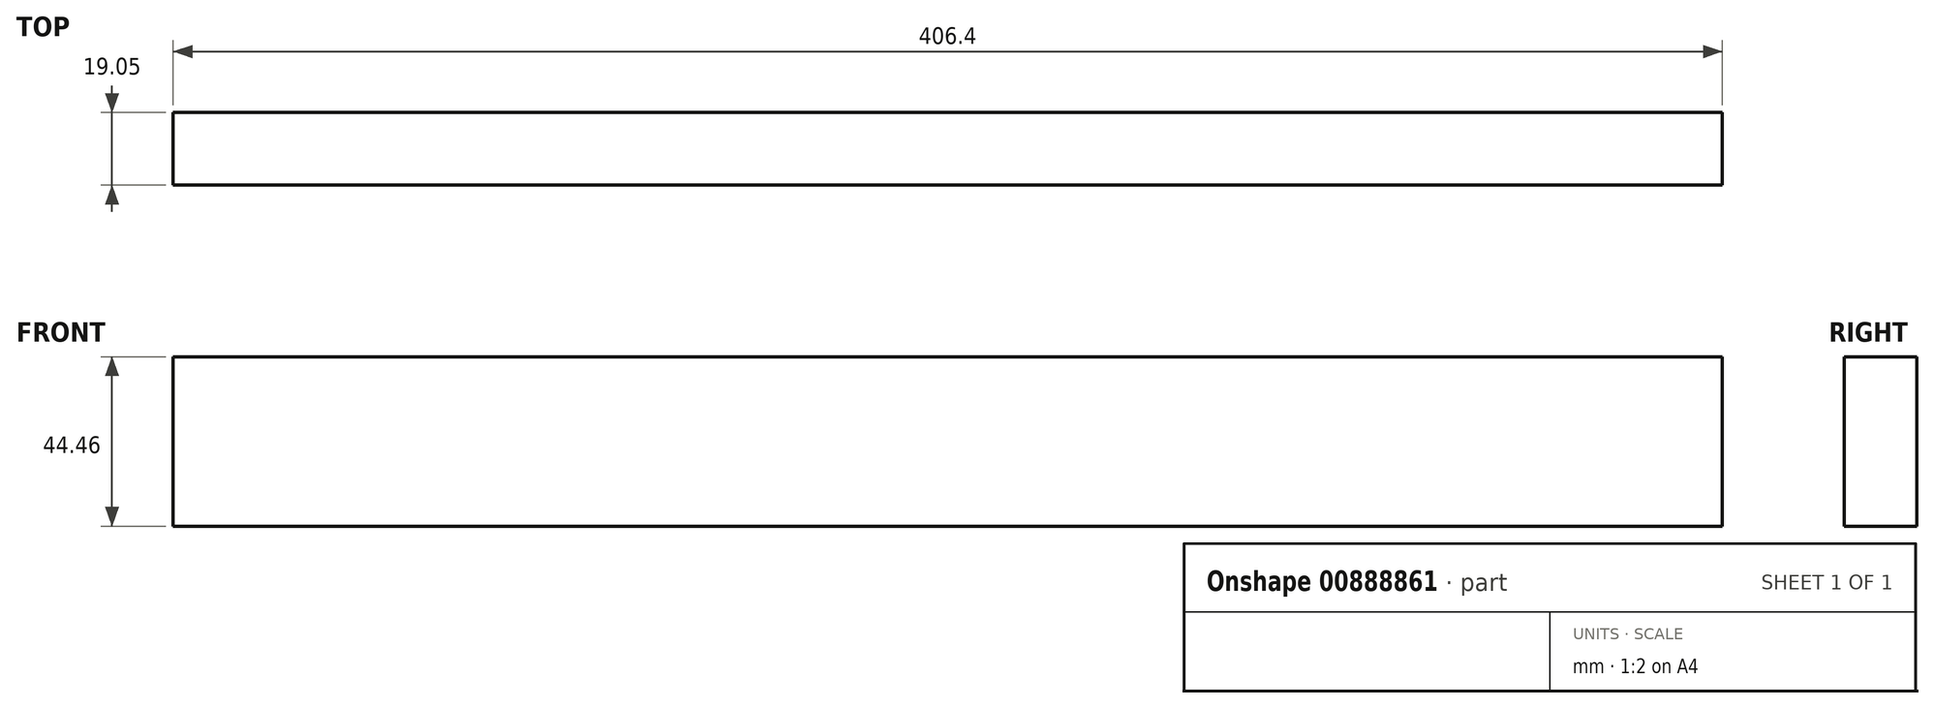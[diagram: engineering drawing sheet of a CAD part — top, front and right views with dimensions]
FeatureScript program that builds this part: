
annotation { "Feature Type Name" : "Feature", "Feature Type Description" : "" }
export const myFeature = defineFeature(function(context is Context, id is Id, definition is map)
    precondition{}
    {
        {
            var Q0;
            Q0=qCreatedBy(makeId("Front.planeOp"),FACE);
            var sketch = newSketch(context, id + "F0", { "sketchPlane" : qUnion([Q0])});
            skLineSegment(sketch, "E0.bottom", {"start": v(203.2, -22.22) * mm, "end": v(-203.2, -22.22) * mm});
            skLineSegment(sketch, "E0.top", {"start": v(203.2, 22.23) * mm, "end": v(-203.2, 22.23) * mm});
            skLineSegment(sketch, "E0.left", {"start": v(203.2, -22.22) * mm, "end": v(203.2, 22.23) * mm});
            skLineSegment(sketch, "E0.right", {"start": v(-203.2, -22.22) * mm, "end": v(-203.2, 22.23) * mm});
            skPoint(sketch, "E0.middle", {"position": v(0, 0) * mm});
            skSolve(sketch);
        }
        {
            var Q0;
            Q0=makeQuery(id+"F0.imprint","IMPRINT",FACE,{"disambiguationData":[TD([[makeQuery(id+"F0.imprint","IMPRINT",EDGE,{"derivedFrom":sQuery(id+"F0.wireOp",EDGE,"E0.bottom")}),-1.0]])]});
            extrude(context, id + "F1", {"entities" : qUnion([Q0]), "depth" : 19.05 * mm, "offsetDistance" : 25.4 * mm});
        }
    });
